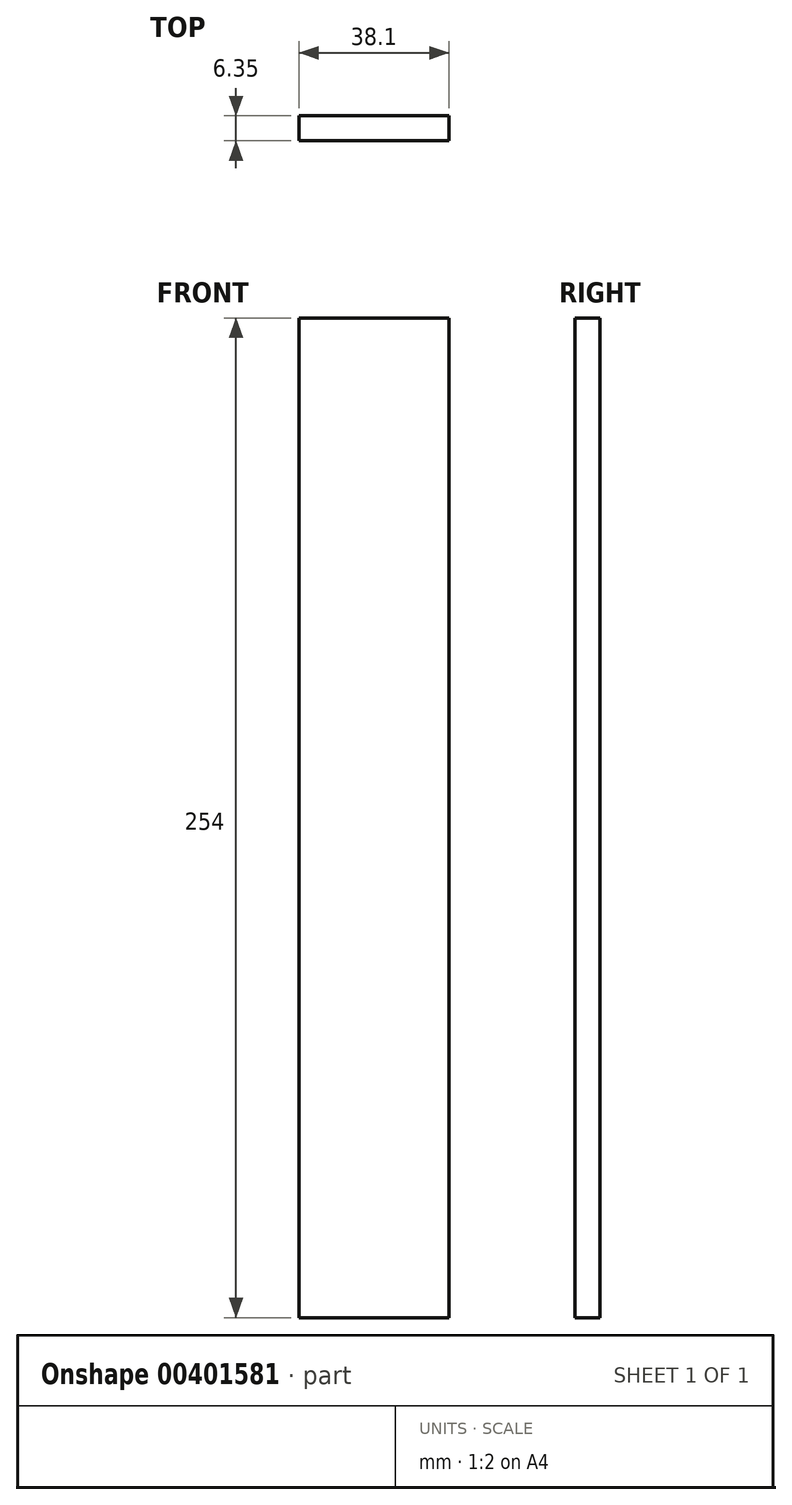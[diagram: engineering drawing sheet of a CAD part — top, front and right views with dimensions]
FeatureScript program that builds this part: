
annotation { "Feature Type Name" : "Feature", "Feature Type Description" : "" }
export const myFeature = defineFeature(function(context is Context, id is Id, definition is map)
    precondition{}
    {
        {
            var Q0;
            Q0=qCreatedBy(makeId("Front.planeOp"),FACE);
            var sketch = newSketch(context, id + "F0", { "sketchPlane" : qUnion([Q0])});
            skLineSegment(sketch, "E0.bottom", {"start": v(61.43, 174.39) * mm, "end": v(23.33, 174.39) * mm});
            skLineSegment(sketch, "E0.top", {"start": v(61.43, -79.61) * mm, "end": v(23.33, -79.61) * mm});
            skLineSegment(sketch, "E0.left", {"start": v(61.43, 174.39) * mm, "end": v(61.43, -79.61) * mm});
            skLineSegment(sketch, "E0.right", {"start": v(23.33, 174.39) * mm, "end": v(23.33, -79.61) * mm});
            skSolve(sketch);
        }
        {
            var Q0;
            Q0 = qSketchRegion(id + "F0", true);
            extrude(context, id + "F1", {"entities" : qUnion([Q0]), "depth" : 6.35 * mm});
        }
    });
